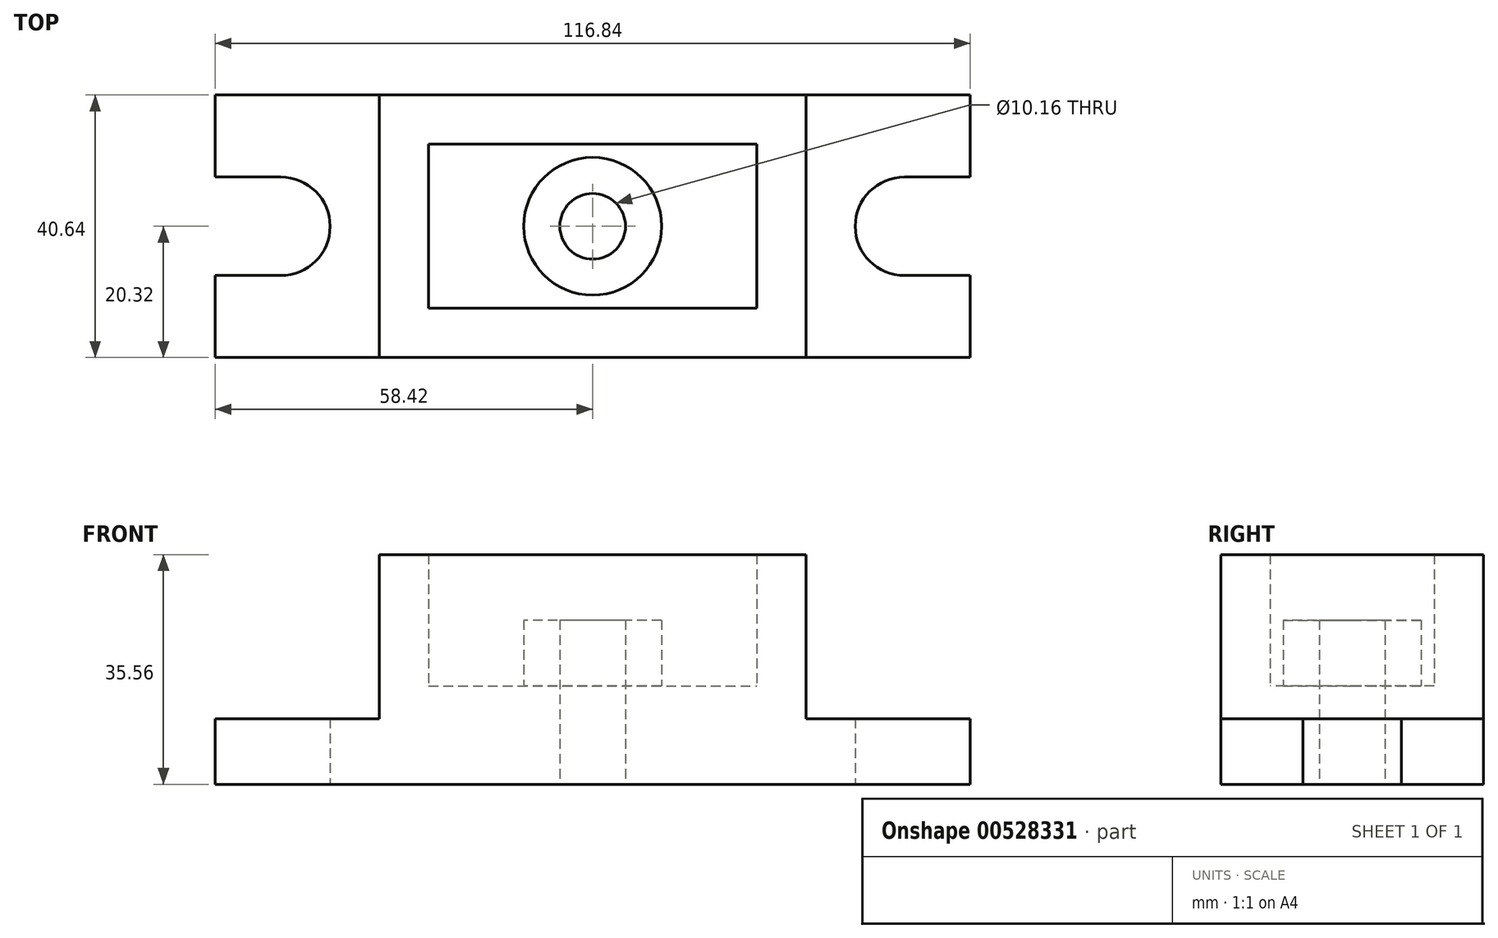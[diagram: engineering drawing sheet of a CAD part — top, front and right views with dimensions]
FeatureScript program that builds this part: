
annotation { "Feature Type Name" : "Feature", "Feature Type Description" : "" }
export const myFeature = defineFeature(function(context is Context, id is Id, definition is map)
    precondition{}
    {
        {
            var Q0;
            Q0=qCreatedBy(makeId("Top.planeOp"),FACE);
            var sketch = newSketch(context, id + "F0", { "sketchPlane" : qUnion([Q0])});
            skLineSegment(sketch, "E0", {"start": v(0, 0) * mm, "end": v(-58.42, 0) * mm});
            skLineSegment(sketch, "E1", {"start": v(0, 0) * mm, "end": v(0, -12.7) * mm});
            skLineSegment(sketch, "E2", {"start": v(0, -12.7) * mm, "end": v(-10.16, -12.7) * mm});
            skArc(sketch, "E3", {"start": v(-10.16, -12.7) * mm, "mid": v(-15.55, -14.93) * mm, "end": v(-17.78, -20.32) * mm});
            skLineSegment(sketch, "E4", {"start": v(-10.16, -12.7) * mm, "end": v(-10.16, -20.32) * mm, "construction": true});
            skLineSegment(sketch, "E5", {"start": v(-10.16, -20.32) * mm, "end": v(-17.78, -20.32) * mm, "construction": true});
            skLineSegment(sketch, "E6", {"start": v(-58.42, 0) * mm, "end": v(-25.4, 0) * mm, "construction": true});
            skLineSegment(sketch, "E7", {"start": v(-25.4, 0) * mm, "end": v(-25.4, -20.32) * mm});
            skLineSegment(sketch, "E8", {"start": v(-25.4, -20.32) * mm, "end": v(-33.02, -20.32) * mm, "construction": true});
            skLineSegment(sketch, "E9", {"start": v(-33.02, -20.32) * mm, "end": v(-33.02, -7.62) * mm});
            skLineSegment(sketch, "E10", {"start": v(-33.02, -7.62) * mm, "end": v(-58.42, -7.62) * mm});
            skLineSegment(sketch, "E11", {"start": v(-58.42, -7.62) * mm, "end": v(-58.42, 0) * mm, "construction": true});
            skLineSegment(sketch, "E12", {"start": v(-25.4, -20.32) * mm, "end": v(-17.78, -20.32) * mm, "construction": true});
            skLineSegment(sketch, "E13.MirrorCS", {"start": v(0, -40.64) * mm, "end": v(-58.42, -40.64) * mm});
            skLineSegment(sketch, "E14.MirrorCS", {"start": v(-33.02, -33.02) * mm, "end": v(-58.42, -33.02) * mm});
            skLineSegment(sketch, "E15.MirrorCS", {"start": v(-33.02, -20.32) * mm, "end": v(-33.02, -33.02) * mm});
            skLineSegment(sketch, "E16.MirrorCS", {"start": v(-58.42, -40.64) * mm, "end": v(-25.4, -40.64) * mm, "construction": true});
            skArc(sketch, "E17.MirrorCS", {"start": v(-10.16, -27.94) * mm, "mid": v(-15.55, -25.7) * mm, "end": v(-17.78, -20.32) * mm});
            skLineSegment(sketch, "E18.MirrorCS", {"start": v(-25.4, -40.64) * mm, "end": v(-25.4, -20.32) * mm});
            skLineSegment(sketch, "E19.MirrorCS", {"start": v(-10.16, -27.94) * mm, "end": v(-10.16, -20.32) * mm, "construction": true});
            skLineSegment(sketch, "E20.MirrorCS", {"start": v(0, -27.94) * mm, "end": v(-10.16, -27.94) * mm});
            skLineSegment(sketch, "E21.MirrorCS", {"start": v(-58.42, -33.02) * mm, "end": v(-58.42, -40.64) * mm, "construction": true});
            skLineSegment(sketch, "E22.MirrorCS", {"start": v(0, -40.64) * mm, "end": v(0, -27.94) * mm});
            skLineSegment(sketch, "E23.MirrorCS", {"start": v(-91.44, -20.32) * mm, "end": v(-83.82, -20.32) * mm, "construction": true});
            skLineSegment(sketch, "E24.MirrorCS", {"start": v(-106.68, -20.32) * mm, "end": v(-99.06, -20.32) * mm, "construction": true});
            skLineSegment(sketch, "E25.MirrorCS", {"start": v(-58.42, -40.64) * mm, "end": v(-91.44, -40.64) * mm, "construction": true});
            skLineSegment(sketch, "E26.MirrorCS", {"start": v(-116.84, 0) * mm, "end": v(-116.84, -12.7) * mm});
            skLineSegment(sketch, "E27.MirrorCS", {"start": v(-106.68, -12.7) * mm, "end": v(-106.68, -20.32) * mm, "construction": true});
            skLineSegment(sketch, "E28.MirrorCS", {"start": v(-91.44, -40.64) * mm, "end": v(-91.44, -20.32) * mm});
            skLineSegment(sketch, "E29.MirrorCS", {"start": v(-116.84, 0) * mm, "end": v(-58.42, 0) * mm});
            skLineSegment(sketch, "E30.MirrorCS", {"start": v(-116.84, -27.94) * mm, "end": v(-106.68, -27.94) * mm});
            skLineSegment(sketch, "E31.MirrorCS", {"start": v(-116.84, -12.7) * mm, "end": v(-106.68, -12.7) * mm});
            skLineSegment(sketch, "E32.MirrorCS", {"start": v(-91.44, -20.32) * mm, "end": v(-99.06, -20.32) * mm, "construction": true});
            skArc(sketch, "E33.MirrorCS", {"start": v(-106.68, -12.7) * mm, "mid": v(-101.3, -14.93) * mm, "end": v(-99.06, -20.32) * mm});
            skLineSegment(sketch, "E34.MirrorCS", {"start": v(-83.82, -7.62) * mm, "end": v(-58.42, -7.62) * mm});
            skLineSegment(sketch, "E35.MirrorCS", {"start": v(-106.68, -27.94) * mm, "end": v(-106.68, -20.32) * mm, "construction": true});
            skArc(sketch, "E36.MirrorCS", {"start": v(-106.68, -27.94) * mm, "mid": v(-101.3, -25.7) * mm, "end": v(-99.06, -20.32) * mm});
            skLineSegment(sketch, "E37.MirrorCS", {"start": v(-83.82, -33.02) * mm, "end": v(-58.42, -33.02) * mm});
            skLineSegment(sketch, "E38.MirrorCS", {"start": v(-58.42, 0) * mm, "end": v(-91.44, 0) * mm, "construction": true});
            skLineSegment(sketch, "E39.MirrorCS", {"start": v(-91.44, 0) * mm, "end": v(-91.44, -20.32) * mm});
            skLineSegment(sketch, "E40.MirrorCS", {"start": v(-116.84, -40.64) * mm, "end": v(-116.84, -27.94) * mm});
            skLineSegment(sketch, "E41.MirrorCS", {"start": v(-83.82, -20.32) * mm, "end": v(-83.82, -33.02) * mm});
            skLineSegment(sketch, "E42.MirrorCS", {"start": v(-83.82, -20.32) * mm, "end": v(-83.82, -7.62) * mm});
            skLineSegment(sketch, "E43.MirrorCS", {"start": v(-116.84, -40.64) * mm, "end": v(-58.42, -40.64) * mm});
            skLineSegment(sketch, "E44", {"start": v(-58.42, -7.62) * mm, "end": v(-58.42, -33.02) * mm});
            skCircle(sketch, "E45", {"center": v(-58.42, -20.32) * mm, "radius": 10.67 * mm});
            skCircle(sketch, "E46", {"center": v(-58.42, -20.32) * mm, "radius": 5.08 * mm});
            skSolve(sketch);
        }
        {
            var Q0;
            {var subQ1=sQuery(id+"F0.wireOp",EDGE,"E26.MirrorCS");Q0=makeQuery(id+"F0.imprint","IMPRINT",FACE,{"disambiguationData":[TD([[makeQuery(id+"F0.imprint","IMPRINT",EDGE,{"derivedFrom":subQ1}),1.0]])]});}
            var Q1;
            {var subQ1=sQuery(id+"F0.wireOp",EDGE,"E1");Q1=makeQuery(id+"F0.imprint","IMPRINT",FACE,{"disambiguationData":[TD([[makeQuery(id+"F0.imprint","IMPRINT",EDGE,{"derivedFrom":subQ1}),-1.0]])]});}
            extrude(context, id + "F1", {"entities" : qUnion([Q0, Q1]), "depth" : 10.16 * mm, "offsetDistance" : 25.4 * mm});
        }
        {
            var Q0;
            {var subQ8=sQuery(id+"F0.wireOp",EDGE,"E7");Q0=makeQuery(id+"F0.imprint","IMPRINT",FACE,{"disambiguationData":[TD([[makeQuery(id+"F0.imprint","IMPRINT",EDGE,{"derivedFrom":subQ8}),-1.0]])]});}
            extrude(context, id + "F2", {"entities" : qUnion([Q0]), "operationType" : NewBodyOperationType.ADD, "depth" : 35.56 * mm, "offsetDistance" : 25.4 * mm});
        }
        {
            var Q0;
            {var subQ4=sQuery(id+"F0.wireOp",EDGE,"E34.MirrorCS");Q0=makeQuery(id+"F0.imprint","IMPRINT",FACE,{"disambiguationData":[TD([[makeQuery(id+"F0.imprint","IMPRINT",EDGE,{"derivedFrom":subQ4}),-1.0]])]});}
            var Q1;
            Q1=makeQuery(id+"F0.imprint","IMPRINT",FACE,{"disambiguationData":[TD([[makeQuery(id+"F0.imprint","IMPRINT",EDGE,{"derivedFrom":sQuery(id+"F0.wireOp",EDGE,"E9")}),1.0]])]});
            extrude(context, id + "F3", {"entities" : qUnion([Q0, Q1]), "operationType" : NewBodyOperationType.ADD, "depth" : 15.24 * mm, "offsetDistance" : 25.4 * mm});
        }
        {
            var Q0;
            {var subQ0=sQuery(id+"F0.wireOp",EDGE,"E45");var subQ1=sQuery(id+"F0.wireOp",EDGE,"E44");var subQ2=makeQuery(id+"F0.imprint","INTERSECT",VERTEX,{"disambiguationData":[OD(0.0)],"derivedFrom":[subQ1,subQ0]});Q0=makeQuery(id+"F0.imprint","IMPRINT",FACE,{"disambiguationData":[TD([[makeQuery(id+"F0.imprint","IMPRINT",EDGE,{"disambiguationData":[TD([[subQ2,-1.0]])],"derivedFrom":subQ1}),-1.0]])]});}
            var Q1;
            {var subQ0=sQuery(id+"F0.wireOp",EDGE,"E45");var subQ1=sQuery(id+"F0.wireOp",EDGE,"E44");var subQ2=makeQuery(id+"F0.imprint","INTERSECT",VERTEX,{"disambiguationData":[OD(0.0)],"derivedFrom":[subQ1,subQ0]});Q1=makeQuery(id+"F0.imprint","IMPRINT",FACE,{"disambiguationData":[TD([[makeQuery(id+"F0.imprint","IMPRINT",EDGE,{"disambiguationData":[TD([[subQ2,-1.0]])],"derivedFrom":subQ1}),1.0]])]});}
            extrude(context, id + "F4", {"entities" : qUnion([Q0, Q1]), "operationType" : NewBodyOperationType.ADD, "depth" : 25.4 * mm, "offsetDistance" : 25.4 * mm});
        }
    });
